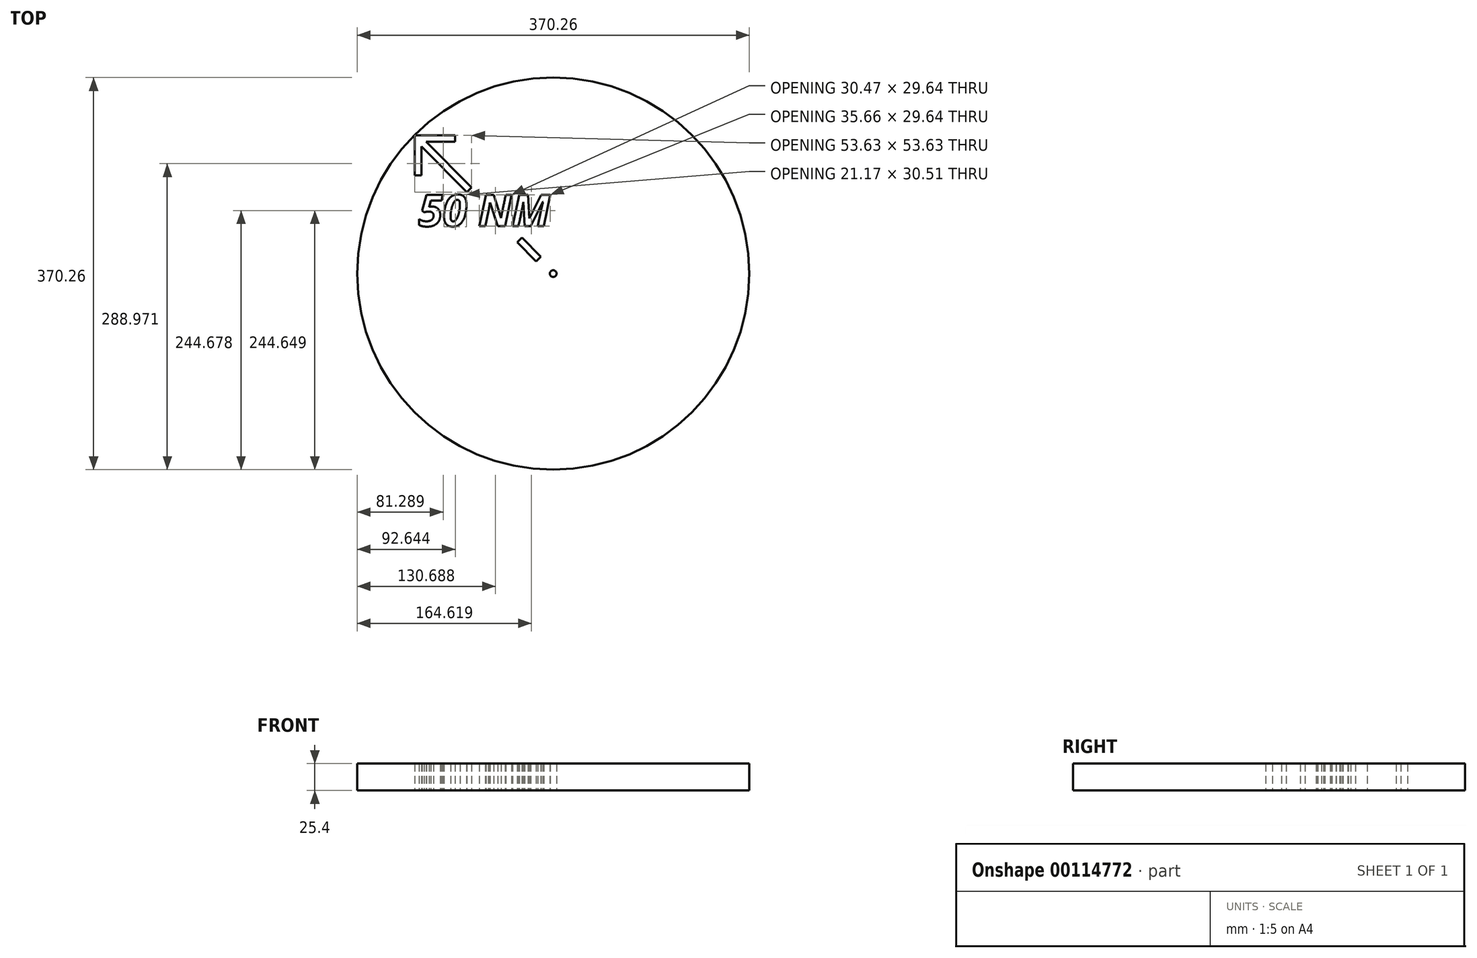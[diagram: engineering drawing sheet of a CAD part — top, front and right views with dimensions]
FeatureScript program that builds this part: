
annotation { "Feature Type Name" : "Feature", "Feature Type Description" : "" }
export const myFeature = defineFeature(function(context is Context, id is Id, definition is map)
    precondition{}
    {
        {
            var Q0;
            Q0=qCreatedBy(makeId("Top.planeOp"),FACE);
            var sketch = newSketch(context, id + "F0", { "sketchPlane" : qUnion([Q0])});
            skCircle(sketch, "E0", {"center": v(0, 0) * mm, "radius": 185.13 * mm});
            skCircle(sketch, "E1", {"center": v(0, 0) * mm, "radius": 3.18 * mm});
            skText(sketch, "E2", { "text": "50 NM", "fontName": "OpenSans-BoldItalic.ttf"});
            skLineSegment(sketch, "E3.0", {"start": v(-120.07, 124.56) * mm, "end": v(-92.8, 124.56) * mm});
            skLineSegment(sketch, "E4.trimOffspring", {"start": v(-133.13, 128.64) * mm, "end": v(-133.15, 128.66) * mm});
            skLineSegment(sketch, "E5.trimOffspring", {"start": v(-128.64, 133.13) * mm, "end": v(-128.66, 133.15) * mm});
            skLineSegment(sketch, "E6.trimOffspring", {"start": v(-124.56, 120.07) * mm, "end": v(-124.56, 92.8) * mm});
            skLineSegment(sketch, "E7", {"start": v(-130.65, 92.8) * mm, "end": v(-124.56, 92.8) * mm});
            skLineSegment(sketch, "E8", {"start": v(-92.8, 124.56) * mm, "end": v(-92.8, 130.65) * mm});
            skLineSegment(sketch, "E9", {"start": v(-81.52, 77.03) * mm, "end": v(-77.03, 81.52) * mm});
            skLineSegment(sketch, "E10.trimOffspring", {"start": v(-81.52, 77.03) * mm, "end": v(-124.56, 120.07) * mm});
            skLineSegment(sketch, "E11.trimOffspring", {"start": v(-77.03, 81.52) * mm, "end": v(-120.07, 124.56) * mm});
            skLineSegment(sketch, "E12.0", {"start": v(-130.65, 130.65) * mm, "end": v(-130.65, 92.8) * mm});
            skLineSegment(sketch, "E13.0", {"start": v(-130.65, 130.65) * mm, "end": v(-92.8, 130.65) * mm});
            skLineSegment(sketch, "E14", {"start": v(-20.53, 25.02) * mm, "end": v(-25.02, 20.53) * mm, "construction": true});
            skLineSegment(sketch, "E15", {"start": v(-16.04, 11.55) * mm, "end": v(-34, 29.51) * mm});
            skLineSegment(sketch, "E16", {"start": v(-34, 29.51) * mm, "end": v(-29.51, 34) * mm});
            skLineSegment(sketch, "E17", {"start": v(-29.51, 34) * mm, "end": v(-11.55, 16.04) * mm});
            skLineSegment(sketch, "E18", {"start": v(-16.04, 11.55) * mm, "end": v(-11.55, 16.04) * mm});
            const initialGuessF0  = {"E2": [-0.12727, 0.0447, 1, 0, 0.02989]};
            skSetInitialGuess(sketch, initialGuessF0);
            skSolve(sketch);
        }
        {
            var Q0;
            Q0=makeQuery(id+"F0.imprint","IMPRINT",FACE,{"disambiguationData":[TD([[makeQuery(id+"F0.imprint","IMPRINT",EDGE,{"derivedFrom":sQuery(id+"F0.wireOp",EDGE,"E1")}),-1.0]])]});
            var Q1;
            Q1=makeQuery(id+"F0.imprint","IMPRINT",FACE,{"disambiguationData":[TD([[makeQuery(id+"F0.imprint","IMPRINT",EDGE,{"derivedFrom":sQuery(id+"F0.wireOp",EDGE,"E2.sketch_text.stroke-29")}),1.0]])]});
            extrude(context, id + "F1", {"entities" : qUnion([Q0, Q1]), "depth" : 25.4 * mm});
        }
    });
